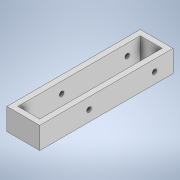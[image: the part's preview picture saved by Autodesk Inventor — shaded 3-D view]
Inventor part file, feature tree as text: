
AUTODESK INVENTOR PART (.ipt)
format: ipt  version: 2022 (Build 260153000, 153)  size: 128,000 bytes
history: native  units: mm
features: extrude x2, sketch x2
ambient origin geometry x8: Origin, YZ Plane, XZ Plane, XY Plane, X Axis, Y Axis, Z Axis, Center Point
bodies: Solid1 (feature_tree)
feature tree (4):
  extrude  "Extrusion1"  Depth=15.0mm
  extrude  "Extrusion2"  Depth=10.0mm
  sketch  "Sketch1"  dims[d0=60.0mm d1=15.0mm]
  sketch  "Sketch2"  dims[d2=5.0mm d3=5.0mm d4=2.5mm d5=2.5mm d6=10.0mm d7=0.0mm d8=10.0mm d9=2.1mm d10=0.0mm d11=0.0mm d12=1.0mm d13=1.0mm d14=20.0mm d15=2.1mm]
